# Revit family: QF_ELECTROLUXPROFESSIONAL_1LSNJ4_IC64821_S
name_source: partatom
category: Attrezzature speciali
units: mm (PartAtom-declared; Revit-internal decimal feet)

## family parameters
Basato su piano di lavoro = No
Condiviso = No
Punto di calcolo locali = No
Quota connettore circolare = Usa diametro
Sempre verticale = Sì
Taglio con vuoti quando caricato = No
Tipo di parte = Normale

## types (3) — shared parameters
Cycle = 50 Hz
Depth Actual = 1110 mm  [stored 3.64173 ft]
Height Actual = 1270 mm  [stored 4.16667 ft]
Latent Heat Output = 0.0
Length Actual = 2775 mm  [stored 9.10433 ft]
Modello = IC64821
Phase = 3
Produttore = Electrolux Professional
Sensible Heat Output = 0.0
Steam Pounds per Hour = 92
URL = www.electroluxprofessional.com
Volts = 400 V
Watts = 1000 W
Weight = 945
zero-valued in all types: Gas KW, Prospetto di default

## per-type parameters (varying)
| type | Descrizione | Item Number |
| 9882030216 | IRONER CYLINDER IC64821 2120MM STEAM CE 400/50/3 4MM SST CYL. ML VAC.FEED.TABLE DIAMMS | 1L0GU4 |
| 9882030249 | IRONER CYLINDER IC64821 2120MM ACTIVE STEAM CE 400/50/3 4MM SST CYL. ML | 1LSPL3 |
| 9882030223 | IRONER CYLINDER IC64821 2120MM STEAM CE 400/50/3 4MM SST CYL. SE, DK, FI VAC.FEED.TABLE DIAMMS | 1L0GUK |

note: [stored X ft] marks values corroborated as IEEE doubles in the binary element streams (Revit-internal decimal feet)

## geometry (parser evidence)
native form markers: Sweep x10
no freeform markers — native parametric forms only
